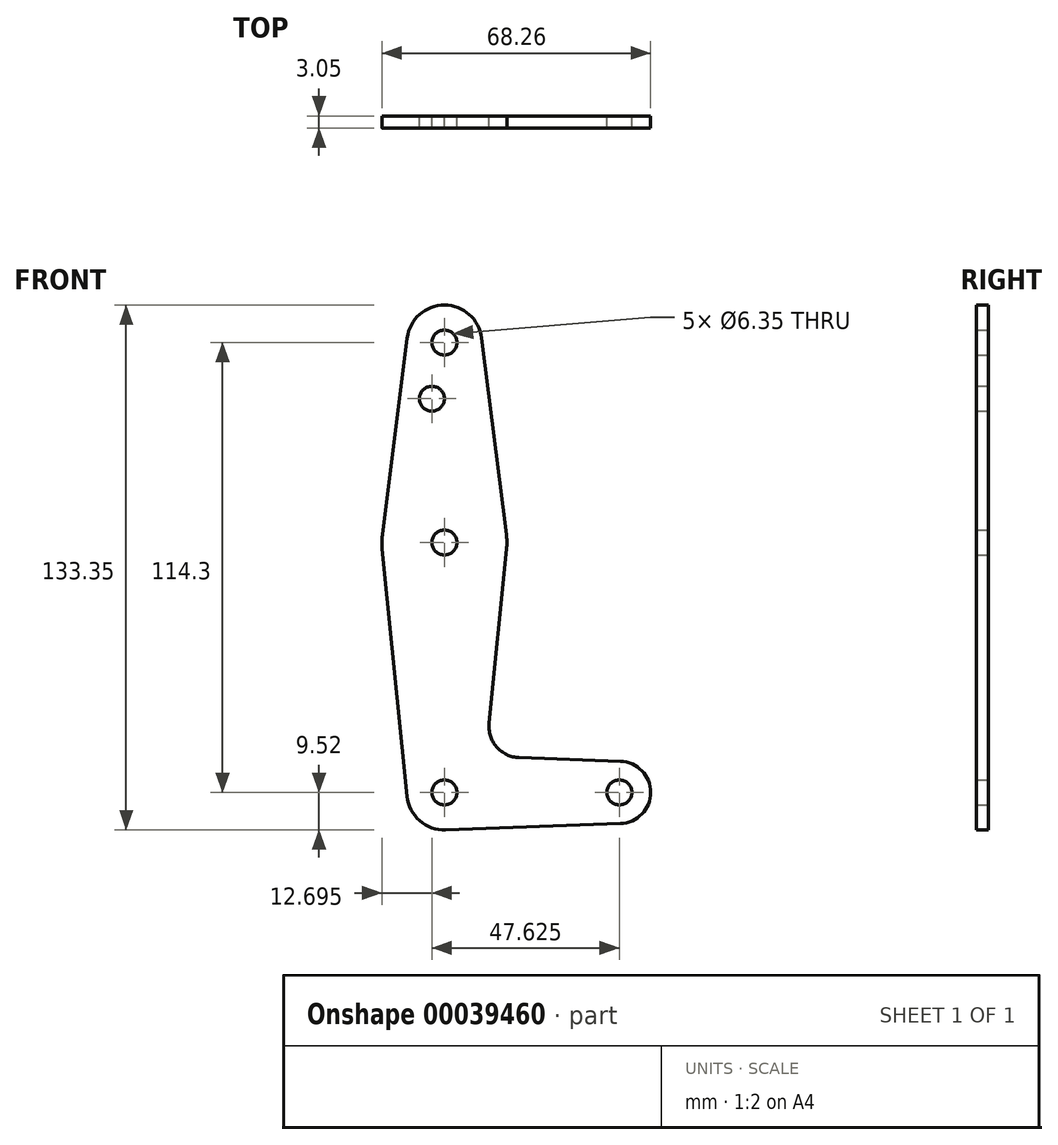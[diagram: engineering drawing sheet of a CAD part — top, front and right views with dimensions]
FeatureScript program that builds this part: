
annotation { "Feature Type Name" : "Feature", "Feature Type Description" : "" }
export const myFeature = defineFeature(function(context is Context, id is Id, definition is map)
    precondition{}
    {
        {
            var Q0;
            Q0=qCreatedBy(makeId("Front.planeOp"),FACE);
            var sketch = newSketch(context, id + "F0", { "sketchPlane" : qUnion([Q0])});
            skCircle(sketch, "E0", {"center": v(0, 0) * mm, "radius": 9.52 * mm});
            skCircle(sketch, "E1", {"center": v(0, 63.5) * mm, "radius": 15.88 * mm});
            skCircle(sketch, "E2", {"center": v(0, 114.3) * mm, "radius": 9.53 * mm});
            skCircle(sketch, "E3", {"center": v(44.45, 0) * mm, "radius": 7.94 * mm});
            skLineSegment(sketch, "E4", {"start": v(0, 114.3) * mm, "end": v(0, 0) * mm, "construction": true});
            skLineSegment(sketch, "E5", {"start": v(0, 0) * mm, "end": v(44.45, 0) * mm, "construction": true});
            skLineSegment(sketch, "E6", {"start": v(-9.45, 115.5) * mm, "end": v(-15.75, 65.48) * mm});
            skLineSegment(sketch, "E7.MirrorCS", {"start": v(9.45, 115.5) * mm, "end": v(15.75, 65.48) * mm});
            skLineSegment(sketch, "E8", {"start": v(-15.8, 61.91) * mm, "end": v(-9.48, -0.95) * mm});
            skLineSegment(sketch, "E9", {"start": v(9.48, -0.95) * mm, "end": v(9.57, 0) * mm});
            skCircle(sketch, "E10", {"center": v(-3.17, 100.03) * mm, "radius": 3.18 * mm});
            skCircle(sketch, "E11", {"center": v(0, 0) * mm, "radius": 3.18 * mm});
            skCircle(sketch, "E12", {"center": v(44.45, 0) * mm, "radius": 3.18 * mm});
            skLineSegment(sketch, "E13", {"start": v(18.97, 8.85) * mm, "end": v(44.73, 7.93) * mm});
            skLineSegment(sketch, "E14", {"start": v(0.34, -9.52) * mm, "end": v(44.73, -7.93) * mm});
            skLineSegment(sketch, "E15.trimOffspring", {"start": v(11.34, 17.6) * mm, "end": v(15.8, 61.91) * mm});
            skPoint(sketch, "E16.visualSharp", {"position": v(10.5, 9.16) * mm});
            skArc(sketch, "E16.filletArc", {"start": v(11.34, 17.6) * mm, "mid": v(13.26, 11.57) * mm, "end": v(18.97, 8.85) * mm});
            skCircle(sketch, "E17", {"center": v(0, 63.5) * mm, "radius": 3.18 * mm});
            skCircle(sketch, "E18", {"center": v(0, 114.3) * mm, "radius": 3.18 * mm});
            skSolve(sketch);
        }
        {
            var Q0;
            Q0 = qSketchRegion(id + "F0", true);
            extrude(context, id + "F1", {"entities" : qUnion([Q0]), "depth" : 3.05 * mm});
        }
    });
